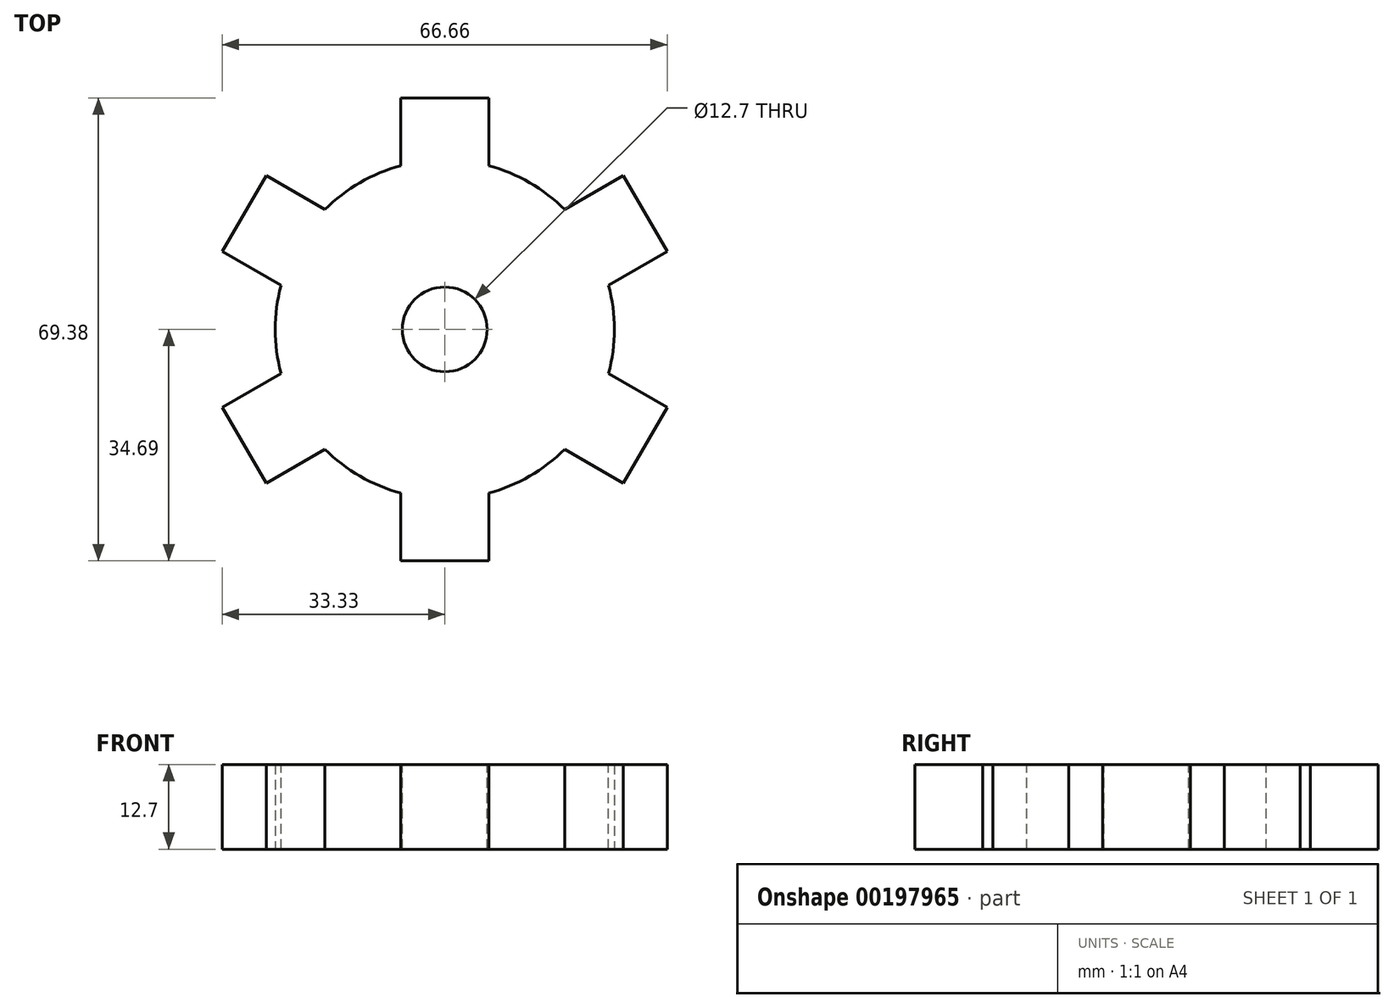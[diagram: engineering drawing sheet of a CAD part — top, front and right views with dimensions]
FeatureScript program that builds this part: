
annotation { "Feature Type Name" : "Feature", "Feature Type Description" : "" }
export const myFeature = defineFeature(function(context is Context, id is Id, definition is map)
    precondition{}
    {
        {
            var Q0;
            Q0=qCreatedBy(makeId("Top.planeOp"),FACE);
            var sketch = newSketch(context, id + "F0", { "sketchPlane" : qUnion([Q0])});
            skCircle(sketch, "E0", {"center": v(0, 0) * mm, "radius": 25.4 * mm});
            skSolve(sketch);
        }
        {
            var Q0;
            Q0 = qSketchRegion(id + "F0", true);
            extrude(context, id + "F1", {"entities" : qUnion([Q0]), "depth" : 12.7 * mm});
        }
        {
            var Q0;
            Q0=makeQuery(id+"F1.opExtrude","CAP_FACE",FACE,{"disambiguationData":[OSD([sQuery(id+"F0.wireOp",EDGE,"E0")])],"isStart":false});
            var sketch = newSketch(context, id + "F2", { "sketchPlane" : qUnion([Q0])});
            skLineSegment(sketch, "E1", {"start": v(0, 0) * mm, "end": v(0, 25.4) * mm});
            skLineSegment(sketch, "E2", {"start": v(0, 0) * mm, "end": v(6.57, 24.53) * mm});
            skLineSegment(sketch, "E3", {"start": v(0, 0) * mm, "end": v(-6.57, 24.53) * mm});
            skLineSegment(sketch, "E4", {"start": v(-6.57, 24.53) * mm, "end": v(6.57, 24.53) * mm});
            skLineSegment(sketch, "E5.0", {"start": v(-6.57, 34.7) * mm, "end": v(6.57, 34.7) * mm});
            skLineSegment(sketch, "E6", {"start": v(-6.57, 34.7) * mm, "end": v(-6.57, 24.53) * mm});
            skLineSegment(sketch, "E7", {"start": v(6.57, 34.7) * mm, "end": v(6.57, 24.53) * mm});
            skSolve(sketch);
        }
        {
            var Q0;
            Q0 = qSketchRegion(id + "F2", true);
            extrude(context, id + "F3", {"entities" : qUnion([Q0]), "operationType" : NewBodyOperationType.ADD, "oppositeDirection" : true, "depth" : 12.7 * mm});
        }
        {
            var Q0;
            Q0=qCreatedBy(makeId("Front.planeOp"),FACE);
            var sketch = newSketch(context, id + "F4", { "sketchPlane" : qUnion([Q0])});
            skLineSegment(sketch, "E8", {"start": v(0, 0) * mm, "end": v(0, 60.6) * mm});
            skSolve(sketch);
        }
        {
            var Q0;
            Q0=makeQuery(id+"F1.opExtrude","SWEPT_BODY",BODY,{"disambiguationData":[OSD([sQuery(id+"F0.wireOp",EDGE,"E0")])]});
            var Q1;
            Q1=sQuery(id+"F4.wireOp",EDGE,"E8");
            circularPattern(context, id + "F5", {"operationType" : NewBodyOperationType.ADD, "entities" : qUnion([Q0]), "axis" : qUnion([Q1]), "angle" : 360 * degree, "instanceCount" : 6, "equalSpace" : true});
        }
        {
            var Q0;
            {var subQ0=makeQuery(id+"F3.boolean.opBoolean","MERGE",FACE,{"derivedFrom":[makeQuery(id+"F1.opExtrude","CAP_FACE",FACE,{"disambiguationData":[OSD([sQuery(id+"F0.wireOp",EDGE,"E0")])],"isStart":false}),makeQuery(id+"F3.opExtrude","CAP_FACE",FACE,{"disambiguationData":[OSD([sQuery(id+"F2.wireOp",EDGE,"E2"),sQuery(id+"F2.wireOp",EDGE,"E3"),sQuery(id+"F2.wireOp",EDGE,"E5.0"),sQuery(id+"F2.wireOp",EDGE,"E6"),sQuery(id+"F2.wireOp",EDGE,"E7")])],"isStart":true})]});Q0=makeQuery(id+"F5.boolean.opBoolean","MERGE",FACE,{"derivedFrom":[subQ0,makeQuery(id+"F5.opPattern","COPY",FACE,{"derivedFrom":subQ0,"instanceName":"1"}),makeQuery(id+"F5.opPattern","COPY",FACE,{"derivedFrom":subQ0,"instanceName":"2"}),makeQuery(id+"F5.opPattern","COPY",FACE,{"derivedFrom":subQ0,"instanceName":"3"}),makeQuery(id+"F5.opPattern","COPY",FACE,{"derivedFrom":subQ0,"instanceName":"4"}),makeQuery(id+"F5.opPattern","COPY",FACE,{"derivedFrom":subQ0,"instanceName":"5"})]});}
            var sketch = newSketch(context, id + "F6", { "sketchPlane" : qUnion([Q0])});
            skCircle(sketch, "E9", {"center": v(0, 0) * mm, "radius": 6.35 * mm});
            skSolve(sketch);
        }
        {
            var Q0;
            Q0 = qSketchRegion(id + "F6", true);
            extrude(context, id + "F7", {"entities" : qUnion([Q0]), "operationType" : NewBodyOperationType.REMOVE, "oppositeDirection" : true, "depth" : 25.4 * mm});
        }
    });
